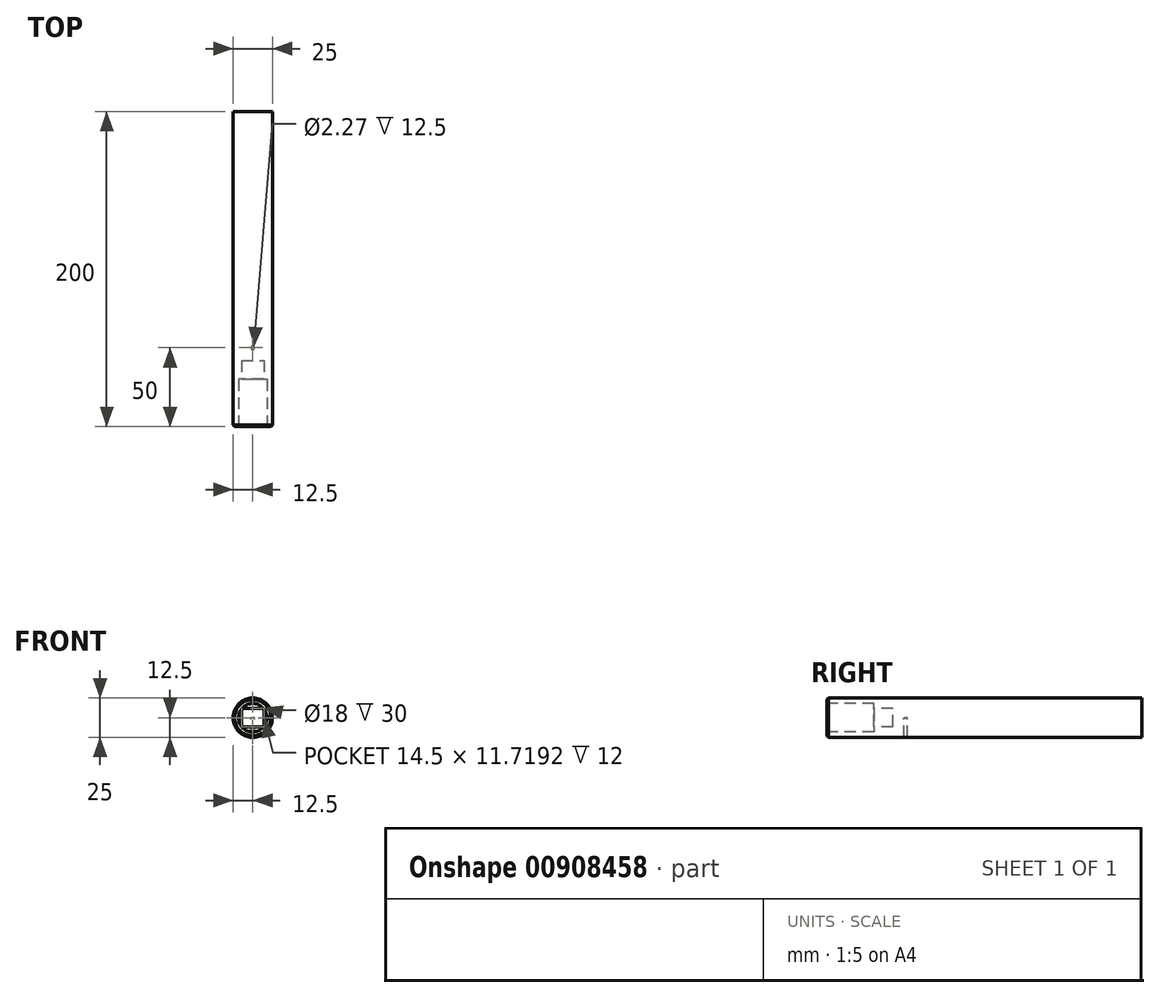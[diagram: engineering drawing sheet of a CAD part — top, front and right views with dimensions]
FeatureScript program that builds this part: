
annotation { "Feature Type Name" : "Feature", "Feature Type Description" : "" }
export const myFeature = defineFeature(function(context is Context, id is Id, definition is map)
    precondition{}
    {
        {
            var Q0;
            Q0=qCreatedBy(makeId("Front.planeOp"),FACE);
            var sketch = newSketch(context, id + "F0", { "sketchPlane" : qUnion([Q0])});
            skCircle(sketch, "E0", {"center": v(0, 0) * mm, "radius": 12.5 * mm});
            skSolve(sketch);
        }
        {
            var Q0;
            Q0 = qSketchRegion(id + "F0", true);
            extrude(context, id + "F1", {"entities" : qUnion([Q0]), "depth" : 200 * mm, "offsetDistance" : 25 * mm});
        }
        {
            var Q0;
            Q0=makeQuery(id+"F1.opExtrude","CAP_FACE",FACE,{"disambiguationData":[OSD([sQuery(id+"F0.wireOp",EDGE,"E0")])],"isStart":false});
            var sketch = newSketch(context, id + "F2", { "sketchPlane" : qUnion([Q0])});
            skCircle(sketch, "E1", {"center": v(0, 0) * mm, "radius": 9 * mm});
            skSolve(sketch);
        }
        {
            var Q0;
            Q0 = qSketchRegion(id + "F2", true);
            extrude(context, id + "F3", {"entities" : qUnion([Q0]), "operationType" : NewBodyOperationType.REMOVE, "oppositeDirection" : true, "depth" : 30 * mm, "offsetDistance" : 25 * mm});
        }
        {
            var Q0;
            Q0=makeQuery(id+"F3.boolean.opBoolean","COPY",FACE,{"derivedFrom":makeQuery(id+"F3.opExtrude","CAP_FACE",FACE,{"disambiguationData":[OSD([sQuery(id+"F2.wireOp",EDGE,"E1")])],"isStart":false})});
            var sketch = newSketch(context, id + "F4", { "sketchPlane" : qUnion([Q0])});
            skLineSegment(sketch, "E2.bottom", {"start": v(-7.25, -5.86) * mm, "end": v(7.25, -5.86) * mm});
            skLineSegment(sketch, "E2.top", {"start": v(-7.25, 5.86) * mm, "end": v(7.25, 5.86) * mm});
            skLineSegment(sketch, "E2.left", {"start": v(-7.25, -5.86) * mm, "end": v(-7.25, 5.86) * mm});
            skLineSegment(sketch, "E2.right", {"start": v(7.25, -5.86) * mm, "end": v(7.25, 5.86) * mm});
            skPoint(sketch, "E2.middle", {"position": v(0, 0) * mm});
            skSolve(sketch);
        }
        {
            var Q0;
            Q0 = qSketchRegion(id + "F4", true);
            extrude(context, id + "F5", {"entities" : qUnion([Q0]), "operationType" : NewBodyOperationType.REMOVE, "oppositeDirection" : true, "depth" : 12 * mm, "offsetDistance" : 25 * mm});
        }
        {
            var Q0;
            Q0=makeQuery(id+"F1.opExtrude","CAP_EDGE",EDGE,{"disambiguationData":[OSD([sQuery(id+"F0.wireOp",EDGE,"E0")])],"isStart":false});
            chamfer(context, id + "F6", {"entities" : qUnion([Q0]), "width" : 1 * mm, "tangentPropagation" : true});
        }
        {
            var Q0;
            Q0=qCreatedBy(makeId("Top.planeOp"),FACE);
            var sketch = newSketch(context, id + "F7", { "sketchPlane" : qUnion([Q0])});
            skCircle(sketch, "E3", {"center": v(0, -150) * mm, "radius": 1.14 * mm});
            skSolve(sketch);
        }
        {
            var Q0;
            Q0 = qSketchRegion(id + "F7", true);
            extrude(context, id + "F8", {"entities" : qUnion([Q0]), "operationType" : NewBodyOperationType.REMOVE, "oppositeDirection" : true, "depth" : 25 * mm, "offsetDistance" : 25 * mm});
        }
    });
